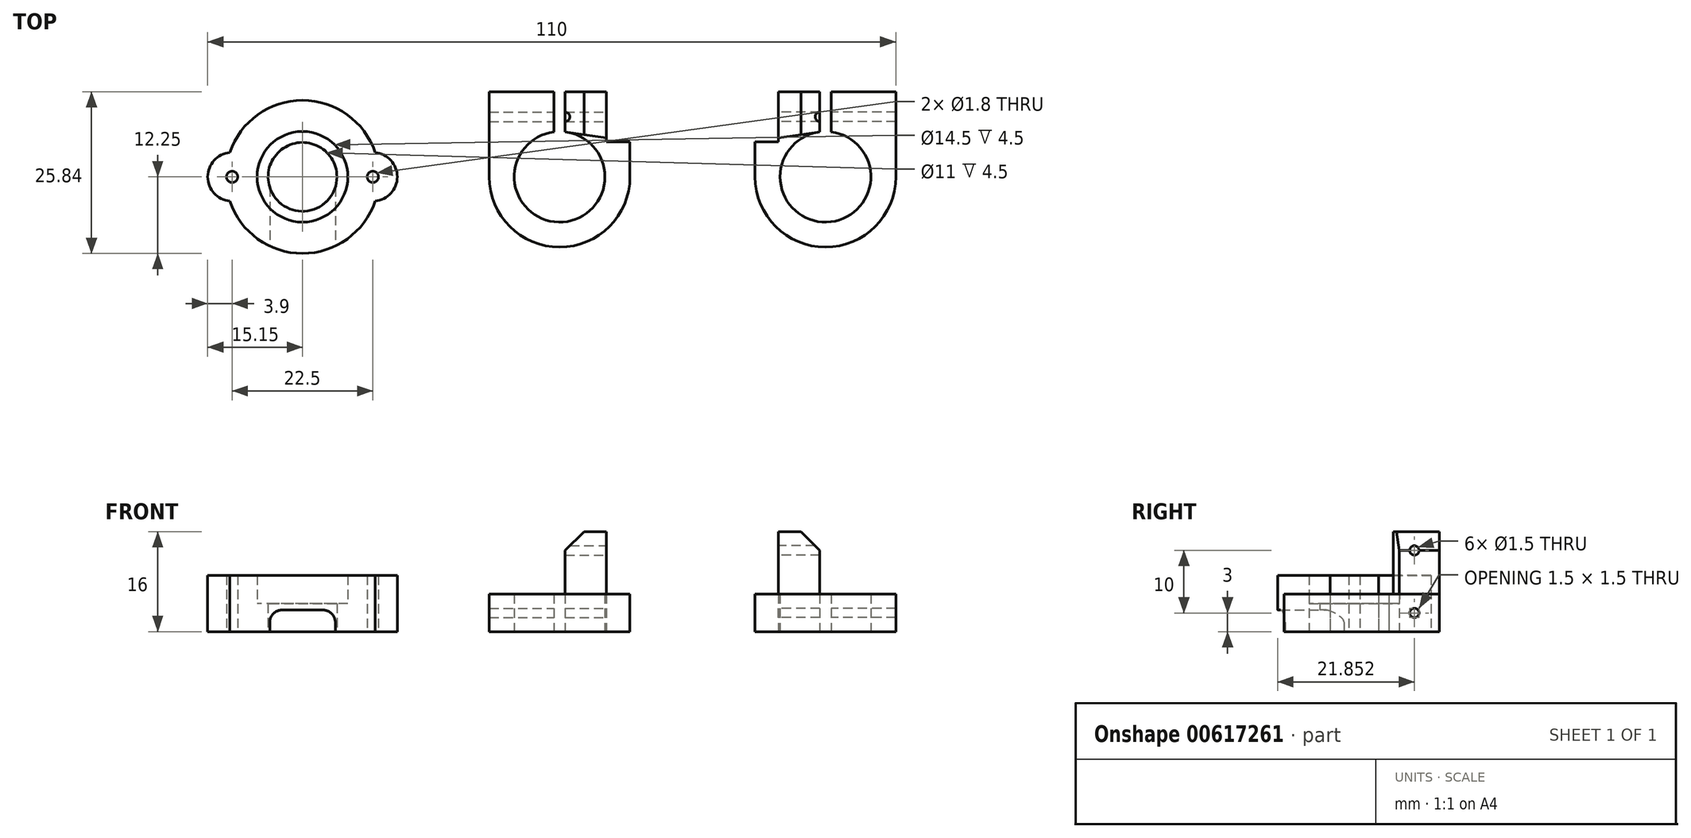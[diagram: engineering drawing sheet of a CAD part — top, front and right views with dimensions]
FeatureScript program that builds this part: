
annotation { "Feature Type Name" : "Feature", "Feature Type Description" : "" }
export const myFeature = defineFeature(function(context is Context, id is Id, definition is map)
    precondition{}
    {
        {
            var Q0;
            Q0=qCreatedBy(makeId("Top.planeOp"),FACE);
            var sketch = newSketch(context, id + "F0", { "sketchPlane" : qUnion([Q0])});
            skCircle(sketch, "E0", {"center": v(0, 0) * mm, "radius": 7.25 * mm});
            skCircle(sketch, "E1.0", {"center": v(0, 0) * mm, "radius": 12.25 * mm});
            skCircle(sketch, "E2", {"center": v(-11.25, 0) * mm, "radius": 0.9 * mm});
            skCircle(sketch, "E3.0", {"center": v(-11.25, 0) * mm, "radius": 3.9 * mm});
            skCircle(sketch, "E4.MirrorC", {"center": v(11.25, 0) * mm, "radius": 0.9 * mm});
            skCircle(sketch, "E5.MirrorC", {"center": v(11.25, 0) * mm, "radius": 3.9 * mm});
            skSolve(sketch);
        }
        {
            var Q0;
            {var subQ0=sQuery(id+"F0.wireOp",EDGE,"E3.0");var subQ1=sQuery(id+"F0.wireOp",EDGE,"E1.0");var subQ2=makeQuery(id+"F0.imprint","INTERSECT",VERTEX,{"disambiguationData":[OD(0.0)],"derivedFrom":[subQ1,subQ0]});Q0=makeQuery(id+"F0.imprint","IMPRINT",FACE,{"disambiguationData":[TD([[makeQuery(id+"F0.imprint","IMPRINT",EDGE,{"disambiguationData":[TD([[subQ2,-1.0]])],"derivedFrom":subQ1}),1.0]])]});}
            var Q1;
            {var subQ0=sQuery(id+"F0.wireOp",EDGE,"E3.0");var subQ1=sQuery(id+"F0.wireOp",EDGE,"E1.0");var subQ2=makeQuery(id+"F0.imprint","INTERSECT",VERTEX,{"disambiguationData":[OD(0.0)],"derivedFrom":[subQ1,subQ0]});Q1=makeQuery(id+"F0.imprint","IMPRINT",FACE,{"disambiguationData":[TD([[makeQuery(id+"F0.imprint","IMPRINT",EDGE,{"disambiguationData":[TD([[subQ2,-1.0]])],"derivedFrom":subQ1}),-1.0]])]});}
            var Q2;
            Q2=makeQuery(id+"F0.imprint","IMPRINT",FACE,{"disambiguationData":[TD([[makeQuery(id+"F0.imprint","IMPRINT",EDGE,{"derivedFrom":sQuery(id+"F0.wireOp",EDGE,"E0")}),-1.0]])]});
            var Q3;
            {var subQ0=sQuery(id+"F0.wireOp",EDGE,"E5.MirrorC");var subQ1=sQuery(id+"F0.wireOp",EDGE,"E1.0");var subQ2=makeQuery(id+"F0.imprint","INTERSECT",VERTEX,{"disambiguationData":[OD(0.0)],"derivedFrom":[subQ1,subQ0]});Q3=makeQuery(id+"F0.imprint","IMPRINT",FACE,{"disambiguationData":[TD([[makeQuery(id+"F0.imprint","IMPRINT",EDGE,{"disambiguationData":[TD([[subQ2,1.0]])],"derivedFrom":subQ1}),1.0]])]});}
            var Q4;
            {var subQ0=sQuery(id+"F0.wireOp",EDGE,"E5.MirrorC");var subQ1=sQuery(id+"F0.wireOp",EDGE,"E1.0");var subQ2=makeQuery(id+"F0.imprint","INTERSECT",VERTEX,{"disambiguationData":[OD(0.0)],"derivedFrom":[subQ1,subQ0]});Q4=makeQuery(id+"F0.imprint","IMPRINT",FACE,{"disambiguationData":[TD([[makeQuery(id+"F0.imprint","IMPRINT",EDGE,{"disambiguationData":[TD([[subQ2,1.0]])],"derivedFrom":subQ1}),-1.0]])]});}
            extrude(context, id + "F1", {"entities" : qUnion([Q0, Q1, Q2, Q3, Q4]), "depth" : 9 * mm, "offsetDistance" : 25 * mm});
        }
        {
            var Q0;
            Q0=makeQuery(id+"F0.imprint","IMPRINT",FACE,{"disambiguationData":[TD([[makeQuery(id+"F0.imprint","IMPRINT",EDGE,{"derivedFrom":sQuery(id+"F0.wireOp",EDGE,"E0")}),1.0]])]});
            extrude(context, id + "F2", {"entities" : qUnion([Q0]), "operationType" : NewBodyOperationType.ADD, "depth" : 4.5 * mm, "offsetDistance" : 25 * mm});
        }
        {
            var Q0;
            Q0=qCreatedBy(makeId("Top.planeOp"),FACE);
            var sketch = newSketch(context, id + "F3", { "sketchPlane" : qUnion([Q0])});
            skCircle(sketch, "E6", {"center": v(0, 0) * mm, "radius": 5.5 * mm});
            skSolve(sketch);
        }
        {
            var Q0;
            Q0 = qSketchRegion(id + "F3", true);
            var Q1;
            Q1=makeQuery(id+"F2.opExtrude","CAP_FACE",FACE,{"disambiguationData":[OSD([sQuery(id+"F0.wireOp",EDGE,"E0")])],"isStart":false});
            extrude(context, id + "F4", {"entities" : qUnion([Q0, Q1]), "operationType" : NewBodyOperationType.REMOVE, "depth" : 25 * mm, "offsetDistance" : 25 * mm});
        }
        {
            var Q0;
            Q0=qCreatedBy(makeId("Front.planeOp"),FACE);
            var sketch = newSketch(context, id + "F5", { "sketchPlane" : qUnion([Q0])});
            skLineSegment(sketch, "E7.bottom", {"start": v(5.24, -3.48) * mm, "end": v(-5.24, -3.48) * mm});
            skLineSegment(sketch, "E7.top", {"start": v(3.24, 3.48) * mm, "end": v(-3.24, 3.48) * mm});
            skLineSegment(sketch, "E7.left", {"start": v(5.24, -3.48) * mm, "end": v(5.24, 1.48) * mm});
            skLineSegment(sketch, "E7.right", {"start": v(-5.24, -3.48) * mm, "end": v(-5.24, 1.48) * mm});
            skPoint(sketch, "E7.middle", {"position": v(0, 0) * mm});
            skPoint(sketch, "E8.visualSharp", {"position": v(-5.24, 3.48) * mm});
            skArc(sketch, "E8.filletArc", {"start": v(-3.24, 3.48) * mm, "mid": v(-4.65, 2.9) * mm, "end": v(-5.24, 1.48) * mm});
            skPoint(sketch, "E9.visualSharp", {"position": v(5.24, 3.48) * mm});
            skArc(sketch, "E9.filletArc", {"start": v(5.24, 1.48) * mm, "mid": v(4.65, 2.9) * mm, "end": v(3.24, 3.48) * mm});
            skSolve(sketch);
        }
        {
            var Q0;
            Q0 = qSketchRegion(id + "F5", true);
            extrude(context, id + "F6", {"entities" : qUnion([Q0]), "operationType" : NewBodyOperationType.REMOVE, "depth" : 25 * mm, "offsetDistance" : 25 * mm});
        }
        {
            var Q0;
            Q0=makeQuery(id+"F1.opExtrude","SWEPT_BODY",BODY,{"disambiguationData":[OSD([sQuery(id+"F0.wireOp",EDGE,"E0"),sQuery(id+"F0.wireOp",EDGE,"E1.0"),sQuery(id+"F0.wireOp",EDGE,"E2"),sQuery(id+"F0.wireOp",EDGE,"E3.0"),sQuery(id+"F0.wireOp",EDGE,"E4.MirrorC"),sQuery(id+"F0.wireOp",EDGE,"E5.MirrorC")])]});
            transform(context, id + "F7", {"entities" : qUnion([Q0]), "transformType" : TransformType.TRANSLATION_3D, "dx" : -41.1 * mm, "dy" : 0 * mm, "dz" : 0 * mm, "makeCopy" : false});
        }
        {
            var Q0;
            Q0=qCreatedBy(makeId("Top.planeOp"),FACE);
            var sketch = newSketch(context, id + "F8", { "sketchPlane" : qUnion([Q0])});
            skCircle(sketch, "E10", {"center": v(0, 0) * mm, "radius": 7.25 * mm});
            skCircle(sketch, "E11.0", {"center": v(0, 0) * mm, "radius": 11.25 * mm});
            skSolve(sketch);
        }
        {
            var Q0;
            Q0=makeQuery(id+"F8.imprint","IMPRINT",FACE,{"disambiguationData":[TD([[makeQuery(id+"F8.imprint","IMPRINT",EDGE,{"derivedFrom":sQuery(id+"F8.wireOp",EDGE,"E10")}),-1.0]])]});
            extrude(context, id + "F9", {"entities" : qUnion([Q0]), "depth" : 6 * mm, "offsetDistance" : 25 * mm});
        }
        {
            var Q0;
            Q0=qCreatedBy(makeId("Top.planeOp"),FACE);
            var sketch = newSketch(context, id + "F10", { "sketchPlane" : qUnion([Q0])});
            skCircle(sketch, "E12", {"center": v(0, 0) * mm, "radius": 7.25 * mm});
            skLineSegment(sketch, "E13.bottom", {"start": v(-11.25, 0) * mm, "end": v(11.25, 0) * mm});
            skLineSegment(sketch, "E13.top", {"start": v(-11.25, 13.6) * mm, "end": v(11.25, 13.6) * mm});
            skLineSegment(sketch, "E13.left", {"start": v(-11.25, 0) * mm, "end": v(-11.25, 13.6) * mm});
            skLineSegment(sketch, "E13.right", {"start": v(11.25, 0) * mm, "end": v(11.25, 13.6) * mm});
            skSolve(sketch);
        }
        {
            var Q0;
            Q0=makeQuery(id+"F10.imprint","IMPRINT",FACE,{"disambiguationData":[TD([[makeQuery(id+"F10.imprint","IMPRINT",EDGE,{"derivedFrom":sQuery(id+"F10.wireOp",EDGE,"E12")}),-1.0]])]});
            var Q1;
            Q1 = qConstructionFilter(qBodyType(qCreatedBy(id + "F10" ,EDGE), BodyType.WIRE), ConstructionObject.NO);
            extrude(context, id + "F11", {"entities" : qUnion([Q0]), "operationType" : NewBodyOperationType.ADD, "surfaceEntities" : qUnion([Q1]), "depth" : 1 * mm, "offsetDistance" : 25 * mm});
        }
        {
            var Q0;
            Q0=makeQuery(id+"F10.imprint","IMPRINT",FACE,{"disambiguationData":[TD([[makeQuery(id+"F10.imprint","IMPRINT",EDGE,{"derivedFrom":sQuery(id+"F10.wireOp",EDGE,"E13.top")}),-1.0]])]});
            extrude(context, id + "F12", {"entities" : qUnion([Q0]), "operationType" : NewBodyOperationType.ADD, "depth" : 6 * mm, "offsetDistance" : 25 * mm});
        }
        {
            var Q0;
            Q0=qCreatedBy(makeId("Top.planeOp"),FACE);
            var sketch = newSketch(context, id + "F13", { "sketchPlane" : qUnion([Q0])});
            skLineSegment(sketch, "E14", {"start": v(0, 0) * mm, "end": v(7.5, 0) * mm, "construction": true});
            skLineSegment(sketch, "E15", {"start": v(7.5, 5.61) * mm, "end": v(7.5, 13.63) * mm});
            skLineSegment(sketch, "E16", {"start": v(7.5, 13.63) * mm, "end": v(7.5, 16) * mm});
            skLineSegment(sketch, "E17", {"start": v(7.5, 16) * mm, "end": v(13.68, 16) * mm});
            skLineSegment(sketch, "E18", {"start": v(13.68, 16) * mm, "end": v(13.68, 5.61) * mm});
            skLineSegment(sketch, "E19", {"start": v(13.68, 5.61) * mm, "end": v(7.5, 5.61) * mm});
            skLineSegment(sketch, "E20.bottom", {"start": v(0.9, 4.96) * mm, "end": v(-0.9, 4.96) * mm});
            skLineSegment(sketch, "E20.top", {"start": v(0.9, 15.47) * mm, "end": v(-0.9, 15.47) * mm});
            skLineSegment(sketch, "E20.left", {"start": v(0.9, 4.96) * mm, "end": v(0.9, 15.47) * mm});
            skLineSegment(sketch, "E20.right", {"start": v(-0.9, 4.96) * mm, "end": v(-0.9, 15.47) * mm});
            skPoint(sketch, "E20.middle", {"position": v(0, 10.21) * mm});
            skSolve(sketch);
        }
        {
            var Q0;
            Q0 = qSketchRegion(id + "F13", true);
            extrude(context, id + "F14", {"entities" : qUnion([Q0]), "operationType" : NewBodyOperationType.REMOVE, "depth" : 25 * mm, "offsetDistance" : 25 * mm});
        }
        {
            var Q0;
            Q0=makeQuery(id+"F14.boolean.opBoolean","COPY",FACE,{"derivedFrom":makeQuery(id+"F14.opExtrude","SWEPT_FACE",FACE,{"disambiguationData":[OSD([sQuery(id+"F13.wireOp",EDGE,"E15"),sQuery(id+"F13.wireOp",EDGE,"E16")])]})});
            var sketch = newSketch(context, id + "F15", { "sketchPlane" : qUnion([Q0])});
            skCircle(sketch, "E21", {"center": v(9.6, 3) * mm, "radius": 0.75 * mm});
            skPoint(sketch, "E21.centerSnap0", {"position": v(13.6, 3) * mm});
            skPoint(sketch, "E21.centerSnap1", {"position": v(9.6, 0) * mm});
            skSolve(sketch);
        }
        {
            var Q0;
            Q0=makeQuery(id+"F12.boolean.opBoolean","MERGE",FACE,{"derivedFrom":[makeQuery(id+"F9.opExtrude","CAP_FACE",FACE,{"disambiguationData":[OSD([sQuery(id+"F8.wireOp",EDGE,"E10"),sQuery(id+"F8.wireOp",EDGE,"E11.0")])],"isStart":false}),makeQuery(id+"F12.opExtrude","CAP_FACE",FACE,{"disambiguationData":[OSD([sQuery(id+"F10.wireOp",EDGE,"E12"),sQuery(id+"F10.wireOp",EDGE,"E13.bottom"),sQuery(id+"F10.wireOp",EDGE,"E13.top"),sQuery(id+"F10.wireOp",EDGE,"E13.left"),sQuery(id+"F10.wireOp",EDGE,"E13.right")])],"isStart":false})]});
            var sketch = newSketch(context, id + "F16", { "sketchPlane" : qUnion([Q0])});
            skLineSegment(sketch, "E22.bottom", {"start": v(7.5, 13.6) * mm, "end": v(4.08, 13.6) * mm});
            skLineSegment(sketch, "E22.left", {"start": v(7.5, 13.6) * mm, "end": v(7.5, 6.22) * mm});
            skLineSegment(sketch, "E23", {"start": v(4.08, 13.6) * mm, "end": v(0.9, 13.6) * mm});
            skLineSegment(sketch, "E24", {"start": v(0.9, 7.2) * mm, "end": v(7.5, 6.22) * mm});
            skPoint(sketch, "E22.top.end.orphan", {"position": v(4.08, 5.61) * mm});
            skLineSegment(sketch, "E25", {"start": v(0.9, 13.6) * mm, "end": v(0.9, 7.2) * mm});
            skSolve(sketch);
        }
        {
            var Q0;
            Q0 = qSketchRegion(id + "F16", true);
            extrude(context, id + "F17", {"entities" : qUnion([Q0]), "operationType" : NewBodyOperationType.ADD, "depth" : 10 * mm, "offsetDistance" : 25 * mm});
        }
        {
            var Q0;
            Q0=makeQuery(id+"F17.opExtrude","CAP_EDGE",EDGE,{"disambiguationData":[OSD([sQuery(id+"F16.wireOp",EDGE,"E25")])],"isStart":false});
            chamfer(context, id + "F18", {"entities" : qUnion([Q0]), "width" : 3 * mm, "tangentPropagation" : true});
        }
        {
            var Q0;
            Q0 = qSketchRegion(id + "F15", true);
            extrude(context, id + "F19", {"entities" : qUnion([Q0]), "operationType" : NewBodyOperationType.REMOVE, "oppositeDirection" : true, "depth" : 25 * mm, "offsetDistance" : 25 * mm});
        }
        {
            var Q0;
            Q0=makeQuery(id+"F17.boolean.opBoolean","MERGE",FACE,{"derivedFrom":[makeQuery(id+"F14.boolean.opBoolean","COPY",FACE,{"derivedFrom":makeQuery(id+"F14.opExtrude","SWEPT_FACE",FACE,{"disambiguationData":[OSD([sQuery(id+"F13.wireOp",EDGE,"E15"),sQuery(id+"F13.wireOp",EDGE,"E16")])]})}),makeQuery(id+"F17.opExtrude","SWEPT_FACE",FACE,{"disambiguationData":[OSD([sQuery(id+"F16.wireOp",EDGE,"E22.left")])]})]});
            var sketch = newSketch(context, id + "F20", { "sketchPlane" : qUnion([Q0])});
            skLineSegment(sketch, "E26", {"start": v(9.6, 3) * mm, "end": v(9.6, 13) * mm, "construction": true});
            skCircle(sketch, "E27", {"center": v(9.6, 13) * mm, "radius": 0.75 * mm});
            skSolve(sketch);
        }
        {
            var Q0;
            Q0 = qSketchRegion(id + "F20", true);
            extrude(context, id + "F21", {"entities" : qUnion([Q0]), "operationType" : NewBodyOperationType.REMOVE, "oppositeDirection" : true, "depth" : 25 * mm, "offsetDistance" : 25 * mm});
        }
        {
            var Q0;
            {var subQ0=sQuery(id+"F10.wireOp",EDGE,"E13.right");Q0=makeQuery(id+"F12.boolean.opBoolean","MERGE",FACE,{"derivedFrom":[makeQuery(id+"F11.opExtrude","SWEPT_FACE",FACE,{"disambiguationData":[OSD([subQ0])]}),makeQuery(id+"F12.opExtrude","SWEPT_FACE",FACE,{"disambiguationData":[OSD([subQ0])]})]});}
            cPlane(context, id + "F22", {"entities" : qUnion([Q0]), "cplaneType" : CPlaneType.OFFSET, "offset" : 10 * mm, "width" : 150 * mm, "height" : 150 * mm});
        }
        {
            var Q0;
            Q0=makeQuery(id+"F9.opExtrude","SWEPT_BODY",BODY,{"disambiguationData":[OSD([sQuery(id+"F8.wireOp",EDGE,"E10"),sQuery(id+"F8.wireOp",EDGE,"E11.0")])]});
            var Q1;
            Q1=qCreatedBy(id+"F22.planeOp",FACE);
            mirror(context, id + "F23", {"entities" : qUnion([Q0]), "mirrorPlane" : qUnion([Q1])});
        }
    });
